# Revit family: BC_Hitachi_Samurai-M-6075_LOD400_
name_source: partatom
category: Mechanical Equipment
revit_build: Autodesk Revit 2018 (Build: 20170223_1515(x64)
units: mm (PartAtom-declared; Revit-internal decimal feet)

## family parameters
Always vertical = Yes
Classification = None
Cut with Voids When Loaded = No
Part Type = Normal
Room Calculation Point = No
Round Connector Dimension = Use Diameter
Shared = No
Work Plane-Based = No

## types (2) — shared parameters
BC_OBJECT_ID = 41997
BC_OBJECT_VERSION = #40
Description = Samurai M - Heat Pump Inverter Scroll. RHMA 18AN - RHMA 100AN
Frequency = 50 Hz
Inlet Water Diameter = 102 mm
Manufacturer = Hitachi Air Conditioning Europe SAS
MasterFormat = Central HVAC Equipment
Masterformat Code = 23 70 00
Model = Samurai M - Heat Pump Inverter Scroll
Nominal Voltage = 400 V
Number of Poles = 3
OmniClass code = 23-33 21 13
OmniClass description = Chillers
Operating mode = Heating+Cooling
Overall height = 2500 mm  [stored 8.2021 ft]
Overall length = 2240 mm  [stored 7.34908 ft]
Overall width = 3050 mm  [stored 10.0066 ft]
Refrigerant Type = R410A
Uniformat = Cooling Generating Systems
Uniformat code = D3030
Water Outlet Diameter = 102 mm

## per-type parameters (varying)
| type | Airflow (High) | BC_VARIANT_ID | Coefficient of Performance (COP) | Cooling Capacity | Cooling Input Rated | Energy efficiency SCOP | Energy efficiency ratio (EER) | Heating Capacity | Heating Input Rated | Load of Refrigerant Fluid | Packing Weight | Rated Cooling Current | SEER energy efficiency | Sound Power (Cooling) | Sound Power (Heating) | Sound Pressure at 10m (Cooling) | Sound Pressure at 1m (Cooling) | Starting current | Weight in operation |
| RHMA 60AN | 17075.8 L/s | 259293 | 3.1 | 159600 W | 50500 W | 3.32 | 3.16 | 160600 W | 51800 W | 29.50 kg | 1895.00 kg | 96 A | 4.24 | 86 | 87 | 57 | 70 | 248 A | 1922.00 kg |
| RHMA 75AN | 18873.6 L/s | 259294 | 3.05 | 188200 W | 61100 W | 3.36 | 3.08 | 190000 W | 62300 W | 32.00 kg | 1974.00 kg | 108 A | 4.28 | 87 | 88 | 58 | 71 | 261 A | 2003.00 kg |

note: column(s) folded — value = type name in every type: Product Code, Reference

note: [stored X ft] marks values corroborated as IEEE doubles in the binary element streams (Revit-internal decimal feet)

## geometry (parser evidence)
native form markers: Blend x2
no freeform markers — native parametric forms only
